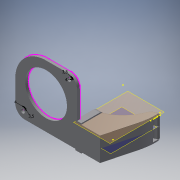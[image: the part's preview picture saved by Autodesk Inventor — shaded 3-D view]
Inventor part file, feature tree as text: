
AUTODESK INVENTOR PART (.ipt)
format: ipt  version: 2016 (Build 200138000, 138)  size: 1,773,056 bytes
history: native  units: mm
features: projected_geometry x31, sketch x28, extrude x25, fillet x11, reference x5, plane x2, chamfer x2, shell x1, imported_body x1, boolean_combine x1, hole x1
ambient origin geometry x8: Origin, YZ Plane, XZ Plane, XY Plane, X Axis, Y Axis, Z Axis, Center Point
bodies: Solid1 (feature_tree), Solid2 (feature_tree)
feature tree (108):
  plane  "Work Plane1"
  extrude  "Extrusion1"  Depth=25.0mm TaperAngle=45.0deg
  chamfer  "Chamfer1"  Distance=2.0mm
  sketch  "Sketch2"  dims[d5=2.0mm]
  shell  "Shell1"  Thickness=3.0mm
  extrude  "Extrusion2"  Depth=2.0mm
  sketch  "Sketch4"  dims[d10=5.5mm d11=2.0mm d12=17.25mm d13=4.0mm d14=16.0mm d15=0.0mm d21=1.0mm d22=0.0mm]
  sketch  "Sketch5"  dims[d23=11.0mm d24=1.0mm d25=45.0deg d26=0.5mm d27=0.0mm]
  fillet  "Fillet1"  Radius=17.25mm
  fillet  "Fillet2"  Radius=4.0mm
  fillet  "Fillet3"  Radius=16.0mm
  fillet  "Fillet4"  Radius=1.0mm
  fillet  "Fillet5"  Radius=0.5mm
  extrude  "Extrusion3"  Depth=3.0mm TaperAngle=0.0deg
  extrude  "Extrusion5"  Depth=4.0mm TaperAngle=0.0deg
  chamfer  "Chamfer2"  Distance=3.0mm
  imported_body  "Base1"
  boolean_combine  "Combine1"
  extrude  "Extrusion6"  Depth=3.0mm TaperAngle=0.0deg
  extrude  "Extrusion7"  Depth=10.0mm
  extrude  "Extrusion8"  Depth=1.0mm TaperAngle=0.0deg
  extrude  "Extrusion9"  Depth=10.0mm
  extrude  "Extrusion10"  Depth=30.0mm
  extrude  "Extrusion11"  Depth=1.0mm TaperAngle=0.0deg
  extrude  "Extrusion12"  Depth=1.0mm TaperAngle=0.0deg
  fillet  "Fillet7"  Radius=0.5mm
  fillet  "Fillet8"  Radius=20.0mm
  fillet  "Fillet11"  Radius=0.1mm
  extrude  "Extrusion13"  Depth=20.0mm TaperAngle=0.0deg
  extrude  "Extrusion14"  Depth=6.0mm
  fillet  "Fillet12"  Radius=8.5mm
  extrude  "Extrusion15"  Depth=0.1mm
  fillet  "Fillet13"  Radius=3.5mm
  plane  "Work Plane2"
  extrude  "Extrusion16"  Depth=4.0mm
  extrude  "Extrusion17"  Depth=2.5mm TaperAngle=0.0deg
  extrude  "Extrusion18"  [1 undecoded]
  extrude  "Extrusion19"  [1 undecoded]
  extrude  "Extrusion20"  [1 undecoded]
  extrude  "Extrusion21"  [1 undecoded]
  extrude  "Extrusion22"  [1 undecoded]
  extrude  "Extrusion23"  [1 undecoded]
  extrude  "Extrusion24"  [1 undecoded]
  extrude  "Extrusion25"  [1 undecoded]
  fillet  "Fillet14"  [1 undecoded]
  sketch  "Sketch29"
  extrude  "Extrusion26"  [1 undecoded]
  hole  "Hole1"  [1 undecoded]
  sketch  "Sketch1"  dims[d0=20.0mm d1=0.0mm d2=25.0mm d3=13.0mm d4=45.0deg]
  sketch  "Sketch3"  dims[d6=8.0mm d7=2.0mm d8=0.0mm d9=3.0mm]
  reference  "Reference1"
  projected_geometry  "Projected Loop1"
  sketch  "Sketch6"  dims[d28=1.0mm d29=3.0mm d30=0.0mm]
  reference  "Reference2"
  reference  "Reference3"
  reference  "Reference4"
  reference  "Reference5"
  sketch  "Sketch8"  dims[d31=4.0mm d32=0.0mm d33=4.0mm d34=0.0mm d36=3.0mm d37=0.0mm]
  projected_geometry  "Projected Loop2"
  sketch  "Sketch9"  dims[d38=3.0mm d39=0.0mm d40=3.0mm d41=0.0mm]
  projected_geometry  "Projected Loop3"
  projected_geometry  "Projected Loop4"
  sketch  "Sketch10"  dims[d42=1.5mm d43=10.0mm]
  projected_geometry  "Projected Loop5"
  projected_geometry  "Projected Loop6"
  sketch  "Sketch11"  dims[d46=3.0mm d47=1.0mm d48=0.0mm]
  projected_geometry  "Projected Loop7"
  sketch  "Sketch12"  dims[d49=20.0mm d50=0.0mm d51=10.0mm]
  projected_geometry  "Projected Loop8"
  sketch  "Sketch13"  dims[d52=20.0mm d53=0.0mm d54=30.0mm]
  projected_geometry  "Projected Loop9"
  sketch  "Sketch14"  dims[d55=7.5mm d56=1.0mm d57=0.0mm]
  projected_geometry  "Projected Loop10"
  projected_geometry  "Projected Loop11"
  projected_geometry  "Projected Loop12"
  sketch  "Sketch15"  dims[d58=1.0mm d59=0.0mm d60=1.0mm d61=0.0mm d62=0.5mm d63=0.0mm d64=20.0mm d65=0.0mm d66=0.1mm d67=0.0mm]
  projected_geometry  "Projected Loop13"
  sketch  "Sketch16"  dims[d68=0.1mm d69=0.0mm d70=20.0mm d71=0.0mm]
  projected_geometry  "Projected Loop14"
  projected_geometry  "Projected Loop15"
  sketch  "Sketch17"  dims[d72=12.566371mm d73=6.0mm d74=8.5mm d75=0.0mm]
  projected_geometry  "Projected Loop16"
  sketch  "Sketch18"  dims[d76=8.5mm d77=0.0mm d78=0.1mm d79=3.5mm]
  projected_geometry  "Projected Loop17"
  sketch  "Sketch19"  dims[d80=3.5mm d81=4.0mm]
  sketch  "Sketch20"  dims[d82=4.0mm d83=2.5mm d84=0.0mm]
  projected_geometry  "Projected Loop18"
  projected_geometry  "Projected Loop19"
  sketch  "Sketch21"  dims[d85=3.5mm d86=6.0mm d87=4.0mm d88=2.0mm d89=90.0deg d90=8.0mm d91=20.594885mm]
  projected_geometry  "Projected Loop20"
  projected_geometry  "Projected Loop21"
  sketch  "Sketch22"
  projected_geometry  "Projected Loop22"
  sketch  "Sketch23"
  projected_geometry  "Projected Loop23"
  sketch  "Sketch24"
  projected_geometry  "Projected Loop24"
  sketch  "Sketch25"
  projected_geometry  "Projected Loop25"
  sketch  "Sketch26"
  projected_geometry  "Projected Loop26"
  sketch  "Sketch27"
  projected_geometry  "Projected Loop27"
  sketch  "Sketch28"
  projected_geometry  "Projected Loop28"
  projected_geometry  "Projected Loop29"
  projected_geometry  "Projected Loop30"
  projected_geometry  "Project Cut Edges1"
note: 11 required parameter values undecoded (feature->parameter linkage not recoverable at this tier; creation-order binding heuristic only, values carry confidence <= 0.55)
